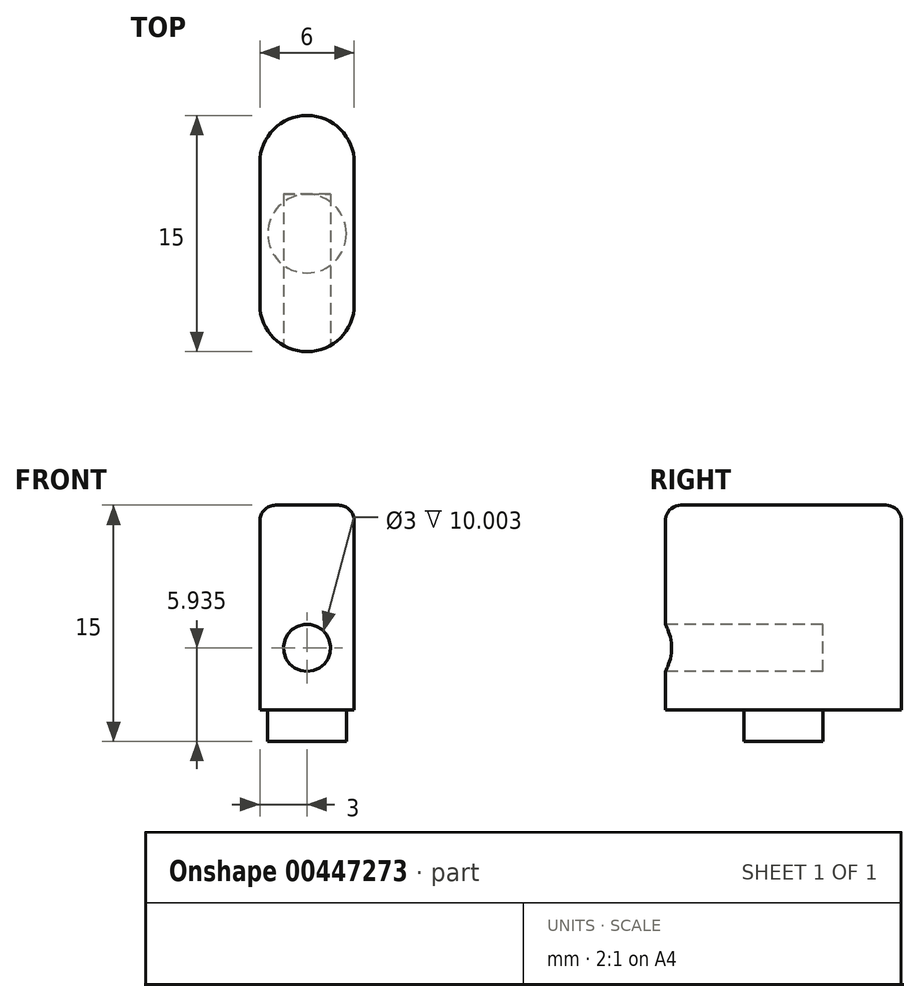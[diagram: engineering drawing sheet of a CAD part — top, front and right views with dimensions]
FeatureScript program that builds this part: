
annotation { "Feature Type Name" : "Feature", "Feature Type Description" : "" }
export const myFeature = defineFeature(function(context is Context, id is Id, definition is map)
    precondition{}
    {
        {
            var Q0;
            Q0=qCreatedBy(makeId("Top.planeOp"),FACE);
            var sketch = newSketch(context, id + "F0", { "sketchPlane" : qUnion([Q0])});
            skLineSegment(sketch, "E0.bottom", {"start": v(-3, 15) * mm, "end": v(3, 15) * mm});
            skLineSegment(sketch, "E0.top", {"start": v(-3, 0) * mm, "end": v(3, 0) * mm});
            skLineSegment(sketch, "E0.left", {"start": v(-3, 15) * mm, "end": v(-3, 0) * mm});
            skLineSegment(sketch, "E0.right", {"start": v(3, 15) * mm, "end": v(3, 0) * mm});
            skPoint(sketch, "E1", {"position": v(0, 15) * mm});
            skSolve(sketch);
        }
        {
            var Q0;
            Q0=makeQuery(id+"F0.imprint","IMPRINT",FACE,{"disambiguationData":[TD([[makeQuery(id+"F0.imprint","IMPRINT",EDGE,{"derivedFrom":sQuery(id+"F0.wireOp",EDGE,"E0.bottom")}),-1.0]])]});
            extrude(context, id + "F1", {"entities" : qUnion([Q0]), "depth" : 13 * mm});
        }
        {
            var Q0;
            Q0=makeQuery(id+"F1.opExtrude","CAP_FACE",FACE,{"disambiguationData":[OSD([sQuery(id+"F0.wireOp",EDGE,"E0.bottom"),sQuery(id+"F0.wireOp",EDGE,"E0.top"),sQuery(id+"F0.wireOp",EDGE,"E0.left"),sQuery(id+"F0.wireOp",EDGE,"E0.right")])],"isStart":true});
            var sketch = newSketch(context, id + "F2", { "sketchPlane" : qUnion([Q0])});
            skLineSegment(sketch, "E2", {"start": v(-3, -7.5) * mm, "end": v(3, -7.5) * mm});
            skCircle(sketch, "E3", {"center": v(0, -7.5) * mm, "radius": 2.5 * mm});
            skSolve(sketch);
        }
        {
            var Q0;
            {var subQ0=sQuery(id+"F2.wireOp",EDGE,"E3");var subQ1=sQuery(id+"F2.wireOp",EDGE,"E2");var subQ2=makeQuery(id+"F2.imprint","INTERSECT",VERTEX,{"disambiguationData":[OD(0.0)],"derivedFrom":[subQ1,subQ0]});Q0=makeQuery(id+"F2.imprint","IMPRINT",FACE,{"disambiguationData":[TD([[makeQuery(id+"F2.imprint","IMPRINT",EDGE,{"disambiguationData":[TD([[subQ2,-1.0]])],"derivedFrom":subQ1}),-1.0]])]});}
            var Q1;
            {var subQ0=sQuery(id+"F2.wireOp",EDGE,"E3");var subQ1=sQuery(id+"F2.wireOp",EDGE,"E2");var subQ2=makeQuery(id+"F2.imprint","INTERSECT",VERTEX,{"disambiguationData":[OD(0.0)],"derivedFrom":[subQ1,subQ0]});Q1=makeQuery(id+"F2.imprint","IMPRINT",FACE,{"disambiguationData":[TD([[makeQuery(id+"F2.imprint","IMPRINT",EDGE,{"disambiguationData":[TD([[subQ2,-1.0]])],"derivedFrom":subQ1}),1.0]])]});}
            extrude(context, id + "F3", {"entities" : qUnion([Q0, Q1]), "operationType" : NewBodyOperationType.ADD, "depth" : 2 * mm});
        }
        {
            var Q0;
            Q0=makeQuery(id+"F1.opExtrude","SWEPT_EDGE",EDGE,{"disambiguationData":[OSD([sQuery(id+"F0.wireOp",EDGE,"E0.top"),sQuery(id+"F0.wireOp",EDGE,"E0.left")])]});
            var Q1;
            Q1=makeQuery(id+"F1.opExtrude","SWEPT_EDGE",EDGE,{"disambiguationData":[OSD([sQuery(id+"F0.wireOp",EDGE,"E0.top"),sQuery(id+"F0.wireOp",EDGE,"E0.right")])]});
            var Q2;
            Q2=makeQuery(id+"F1.opExtrude","SWEPT_EDGE",EDGE,{"disambiguationData":[OSD([sQuery(id+"F0.wireOp",EDGE,"E0.bottom"),sQuery(id+"F0.wireOp",EDGE,"E0.right")])]});
            var Q3;
            Q3=makeQuery(id+"F1.opExtrude","SWEPT_EDGE",EDGE,{"disambiguationData":[OSD([sQuery(id+"F0.wireOp",EDGE,"E0.bottom"),sQuery(id+"F0.wireOp",EDGE,"E0.left")])]});
            fillet(context, id + "F4", {"entities" : qUnion([Q0, Q1, Q2, Q3]), "radius" : 3 * mm, "tangentPropagation" : true, "allowEdgeOverflow" : false});
        }
        {
            var Q0;
            Q0=makeQuery(id+"F1.opExtrude","CAP_FACE",FACE,{"disambiguationData":[OSD([sQuery(id+"F0.wireOp",EDGE,"E0.bottom"),sQuery(id+"F0.wireOp",EDGE,"E0.top"),sQuery(id+"F0.wireOp",EDGE,"E0.left"),sQuery(id+"F0.wireOp",EDGE,"E0.right")])],"isStart":false});
            fillet(context, id + "F5", {"entities" : qUnion([Q0]), "radius" : 1 * mm, "tangentPropagation" : true, "allowEdgeOverflow" : false});
        }
        {
            var Q0;
            Q0=qCreatedBy(makeId("Front.planeOp"),FACE);
            var sketch = newSketch(context, id + "F6", { "sketchPlane" : qUnion([Q0])});
            skCircle(sketch, "E4", {"center": v(0, 3.93) * mm, "radius": 1.5 * mm});
            skSolve(sketch);
        }
        {
            var Q0;
            Q0=makeQuery(id+"F6.imprint","IMPRINT",FACE,{"disambiguationData":[TD([[makeQuery(id+"F6.imprint","IMPRINT",EDGE,{"derivedFrom":sQuery(id+"F6.wireOp",EDGE,"E4")}),1.0]])]});
            extrude(context, id + "F7", {"entities" : qUnion([Q0]), "operationType" : NewBodyOperationType.REMOVE, "oppositeDirection" : true, "depth" : 10 * mm});
        }
    });
